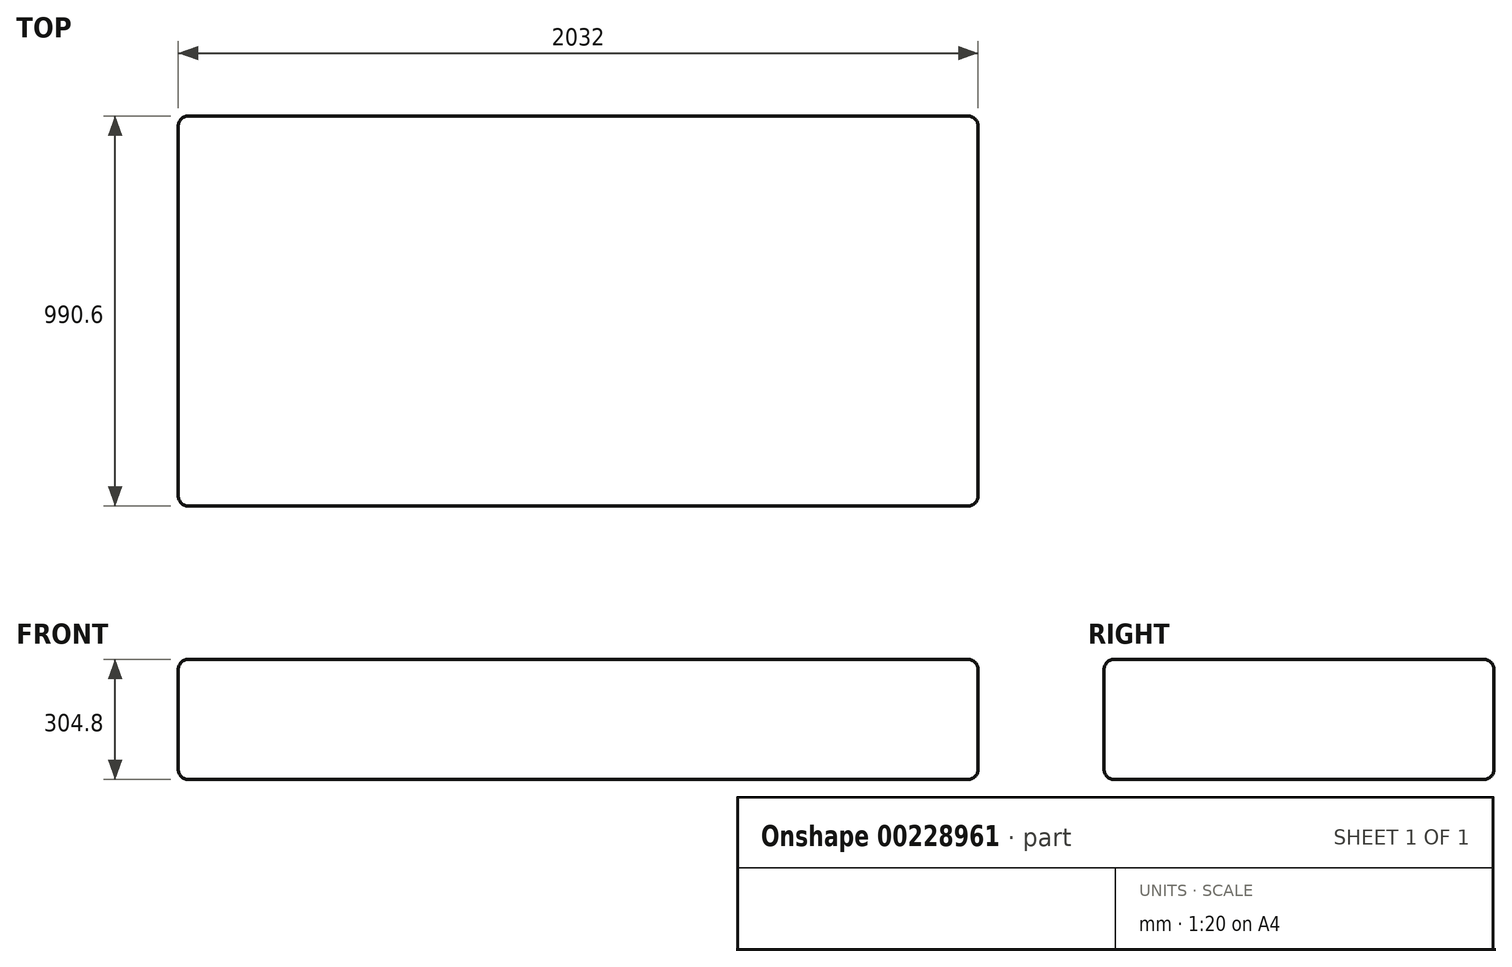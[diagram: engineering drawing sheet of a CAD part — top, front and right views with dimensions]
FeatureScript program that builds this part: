
annotation { "Feature Type Name" : "Feature", "Feature Type Description" : "" }
export const myFeature = defineFeature(function(context is Context, id is Id, definition is map)
    precondition{}
    {
        {
            var Q0;
            Q0=qCreatedBy(makeId("Top.planeOp"),FACE);
            var sketch = newSketch(context, id + "F0", { "sketchPlane" : qUnion([Q0])});
            skLineSegment(sketch, "E0.bottom", {"start": v(-1037.05, 578.73) * mm, "end": v(994.95, 578.73) * mm});
            skLineSegment(sketch, "E0.top", {"start": v(-1037.05, -411.87) * mm, "end": v(994.95, -411.87) * mm});
            skLineSegment(sketch, "E0.left", {"start": v(-1037.05, 578.73) * mm, "end": v(-1037.05, -411.87) * mm});
            skLineSegment(sketch, "E0.right", {"start": v(994.95, 578.73) * mm, "end": v(994.95, -411.87) * mm});
            skSolve(sketch);
        }
        {
            var Q0;
            Q0=makeQuery(id+"F0.imprint","IMPRINT",FACE,{"disambiguationData":[TD([[makeQuery(id+"F0.imprint","IMPRINT",EDGE,{"derivedFrom":sQuery(id+"F0.wireOp",EDGE,"E0.bottom")}),-1.0]])]});
            extrude(context, id + "F1", {"entities" : qUnion([Q0]), "depth" : 304.8 * mm});
        }
        {
            var Q0;
            Q0=makeQuery(id+"F1.opExtrude","CAP_FACE",FACE,{"disambiguationData":[OSD([sQuery(id+"F0.wireOp",EDGE,"E0.bottom"),sQuery(id+"F0.wireOp",EDGE,"E0.top"),sQuery(id+"F0.wireOp",EDGE,"E0.left"),sQuery(id+"F0.wireOp",EDGE,"E0.right")])],"isStart":false});
            var Q1;
            Q1=makeQuery(id+"F1.opExtrude","SWEPT_FACE",FACE,{"disambiguationData":[OSD([sQuery(id+"F0.wireOp",EDGE,"E0.top")])]});
            var Q2;
            Q2=makeQuery(id+"F1.opExtrude","SWEPT_FACE",FACE,{"disambiguationData":[OSD([sQuery(id+"F0.wireOp",EDGE,"E0.right")])]});
            var Q3;
            Q3=makeQuery(id+"F1.opExtrude","SWEPT_FACE",FACE,{"disambiguationData":[OSD([sQuery(id+"F0.wireOp",EDGE,"E0.bottom")])]});
            var Q4;
            Q4=makeQuery(id+"F1.opExtrude","SWEPT_FACE",FACE,{"disambiguationData":[OSD([sQuery(id+"F0.wireOp",EDGE,"E0.left")])]});
            fillet(context, id + "F2", {"entities" : qUnion([Q0, Q1, Q2, Q3, Q4]), "radius" : 25.4 * mm, "tangentPropagation" : true, "allowEdgeOverflow" : false});
        }
    });
